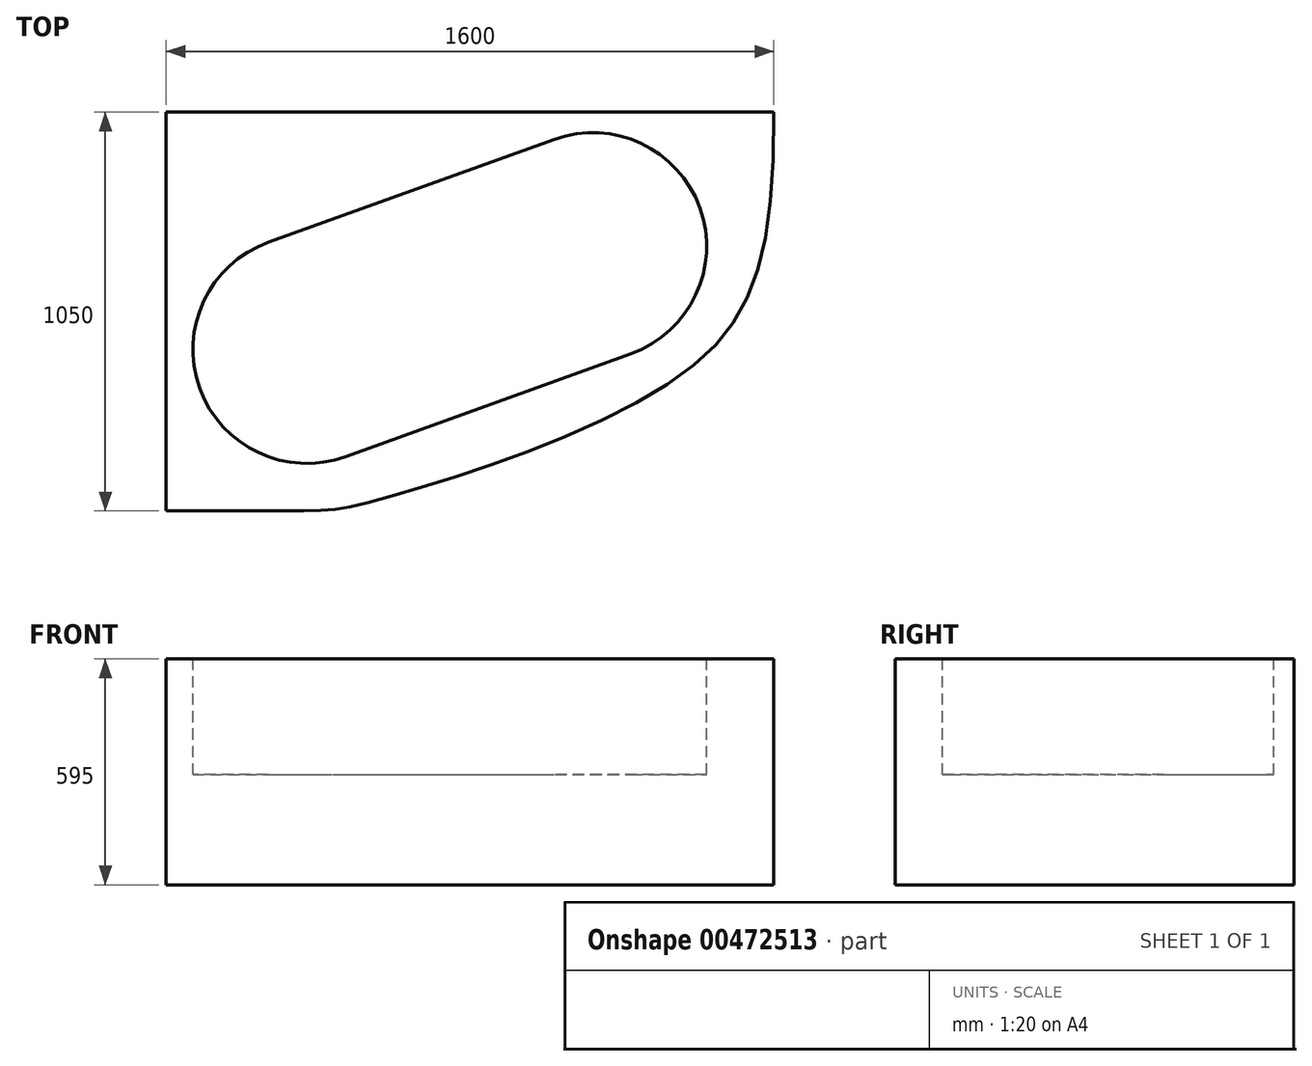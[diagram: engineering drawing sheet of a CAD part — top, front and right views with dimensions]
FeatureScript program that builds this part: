
annotation { "Feature Type Name" : "Feature", "Feature Type Description" : "" }
export const myFeature = defineFeature(function(context is Context, id is Id, definition is map)
    precondition{}
    {
        {
            var Q0;
            Q0=qCreatedBy(makeId("Top.planeOp"),FACE);
            var sketch = newSketch(context, id + "F0", { "sketchPlane" : qUnion([Q0])});
            skLineSegment(sketch, "E0", {"start": v(-818.67, 439.04) * mm, "end": v(781.33, 439.04) * mm});
            skLineSegment(sketch, "E1", {"start": v(-818.67, 439.04) * mm, "end": v(-818.67, -610.96) * mm});
            skLineSegment(sketch, "E2", {"start": v(-818.67, -610.96) * mm, "end": v(-520.29, -610.96) * mm});
            skFitSpline(sketch, "E3", {"points": [v(-520.29, -610.96) * mm, v(-301.1, -592.1) * mm, v(517.68, -267.11) * mm, v(781.33, 439.04) * mm], "startDerivative": vector(1745.5, 2.52) * mm, "endDerivative": vector(-0.1, 3061.4) * mm});
            skSolve(sketch);
        }
        {
            var Q0;
            Q0=makeQuery(id+"F0.imprint","IMPRINT",FACE,{"disambiguationData":[TD([[makeQuery(id+"F0.imprint","IMPRINT",EDGE,{"derivedFrom":sQuery(id+"F0.wireOp",EDGE,"E0")}),-1.0]])]});
            extrude(context, id + "F1", {"entities" : qUnion([Q0]), "depth" : 595 * mm, "offsetDistance" : 25 * mm});
        }
        {
            var Q0;
            Q0=makeQuery(id+"F1.opExtrude","CAP_FACE",FACE,{"disambiguationData":[OSD([sQuery(id+"F0.wireOp",EDGE,"E0"),sQuery(id+"F0.wireOp",EDGE,"E1"),sQuery(id+"F0.wireOp",EDGE,"E2"),sQuery(id+"F0.wireOp",EDGE,"E3")])],"isStart":false});
            var sketch = newSketch(context, id + "F2", { "sketchPlane" : qUnion([Q0])});
            skLineSegment(sketch, "E4", {"start": v(-448.15, -186.07) * mm, "end": v(304.44, 85.24) * mm, "construction": true});
            skArc(sketch, "E5", {"start": v(-549.9, 96.15) * mm, "mid": v(-730.38, -287.81) * mm, "end": v(-346.41, -468.3) * mm});
            skArc(sketch, "E6", {"start": v(406.18, -196.99) * mm, "mid": v(586.66, 186.98) * mm, "end": v(202.7, 367.46) * mm});
            skLineSegment(sketch, "E7", {"start": v(-448.15, -186.07) * mm, "end": v(-549.9, 96.15) * mm, "construction": true});
            skLineSegment(sketch, "E8", {"start": v(304.44, 85.24) * mm, "end": v(202.7, 367.46) * mm, "construction": true});
            skLineSegment(sketch, "E9", {"start": v(-448.15, -186.07) * mm, "end": v(-346.41, -468.3) * mm, "construction": true});
            skLineSegment(sketch, "E10", {"start": v(304.44, 85.24) * mm, "end": v(406.18, -196.99) * mm, "construction": true});
            skLineSegment(sketch, "E11", {"start": v(-549.9, 96.15) * mm, "end": v(202.7, 367.46) * mm});
            skLineSegment(sketch, "E12", {"start": v(-346.41, -468.3) * mm, "end": v(406.18, -196.99) * mm});
            skLineSegment(sketch, "E13", {"start": v(-448.15, -186.07) * mm, "end": v(-730.38, -287.81) * mm, "construction": true});
            skLineSegment(sketch, "E14", {"start": v(304.44, 85.24) * mm, "end": v(586.66, 186.98) * mm, "construction": true});
            skSolve(sketch);
        }
        {
            var Q0;
            Q0=makeQuery(id+"F2.imprint","IMPRINT",FACE,{"disambiguationData":[TD([[makeQuery(id+"F2.imprint","IMPRINT",EDGE,{"derivedFrom":sQuery(id+"F2.wireOp",EDGE,"E5")}),1.0]])]});
            extrude(context, id + "F3", {"entities" : qUnion([Q0]), "operationType" : NewBodyOperationType.REMOVE, "oppositeDirection" : true, "depth" : 305 * mm, "offsetDistance" : 25 * mm});
        }
    });
